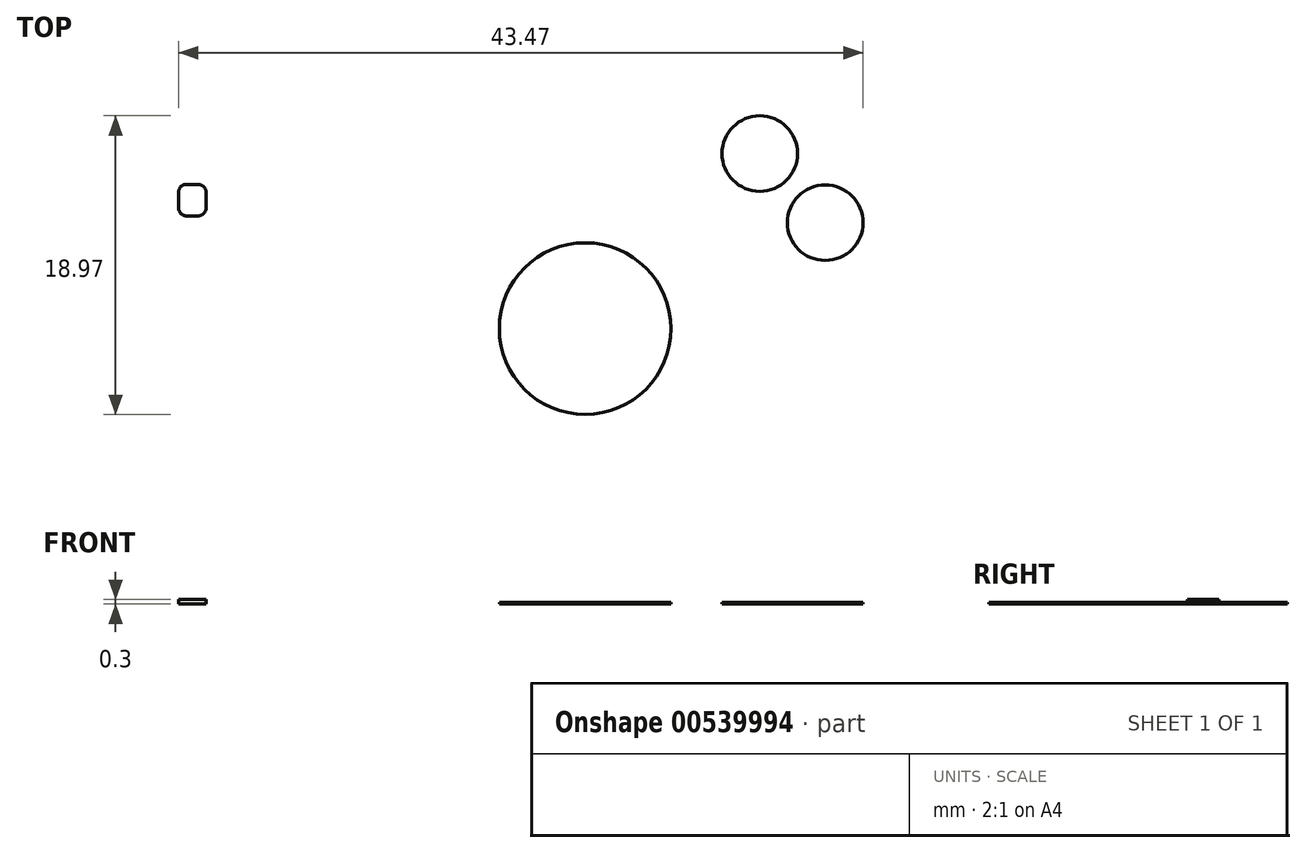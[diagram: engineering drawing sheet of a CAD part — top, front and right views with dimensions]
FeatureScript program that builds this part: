
annotation { "Feature Type Name" : "Feature", "Feature Type Description" : "" }
export const myFeature = defineFeature(function(context is Context, id is Id, definition is map)
    precondition{}
    {
        {
            var Q0;
            Q0=qCreatedBy(makeId("Top.planeOp"),FACE);
            var sketch = newSketch(context, id + "F0", { "sketchPlane" : qUnion([Q0])});
            skCircle(sketch, "E0", {"center": v(0, 0) * mm, "radius": 5.45 * mm});
            skSolve(sketch);
        }
        {
            var Q0;
            Q0 = qSketchRegion(id + "F0", true);
            extrude(context, id + "F1", {"entities" : qUnion([Q0]), "depth" : .1 * mm, "offsetDistance" : 25 * mm});
        }
        {
            var Q0;
            Q0=qCreatedBy(makeId("Top.planeOp"),FACE);
            var sketch = newSketch(context, id + "F2", { "sketchPlane" : qUnion([Q0])});
            skCircle(sketch, "E1", {"center": v(11.1, 11.12) * mm, "radius": 2.4 * mm});
            skCircle(sketch, "E2", {"center": v(15.25, 6.73) * mm, "radius": 2.4 * mm});
            skSolve(sketch);
        }
        {
            var Q0;
            Q0=makeQuery(id+"F2.imprint","IMPRINT",FACE,{"disambiguationData":[TD([[makeQuery(id+"F2.imprint","IMPRINT",EDGE,{"derivedFrom":sQuery(id+"F2.wireOp",EDGE,"E1")}),1.0]])]});
            var Q1;
            Q1=makeQuery(id+"F2.imprint","IMPRINT",FACE,{"disambiguationData":[TD([[makeQuery(id+"F2.imprint","IMPRINT",EDGE,{"derivedFrom":sQuery(id+"F2.wireOp",EDGE,"E2")}),1.0]])]});
            extrude(context, id + "F3", {"entities" : qUnion([Q0, Q1]), "depth" : .1 * mm, "offsetDistance" : 25 * mm});
        }
        {
            var Q0;
            Q0=qCreatedBy(makeId("Top.planeOp"),FACE);
            var sketch = newSketch(context, id + "F4", { "sketchPlane" : qUnion([Q0])});
            skLineSegment(sketch, "E3.bottom", {"start": v(-24.07, 7.16) * mm, "end": v(-25.82, 7.16) * mm});
            skLineSegment(sketch, "E3.top", {"start": v(-24.07, 9.16) * mm, "end": v(-25.82, 9.16) * mm});
            skLineSegment(sketch, "E3.left", {"start": v(-24.07, 7.16) * mm, "end": v(-24.07, 9.16) * mm});
            skLineSegment(sketch, "E3.right", {"start": v(-25.82, 7.16) * mm, "end": v(-25.82, 9.16) * mm});
            skPoint(sketch, "E3.middle", {"position": v(-24.95, 8.16) * mm});
            skLineSegment(sketch, "E4.bottom", {"start": v(-25.82, 9.16) * mm, "end": v(-24.07, 9.16) * mm});
            skLineSegment(sketch, "E4.top", {"start": v(-25.82, 10.56) * mm, "end": v(-24.07, 10.56) * mm});
            skLineSegment(sketch, "E4.left", {"start": v(-25.82, 9.16) * mm, "end": v(-25.82, 10.56) * mm});
            skLineSegment(sketch, "E4.right", {"start": v(-24.07, 9.16) * mm, "end": v(-24.07, 10.56) * mm});
            skLineSegment(sketch, "E5.bottom", {"start": v(-25.82, 7.16) * mm, "end": v(-24.07, 7.16) * mm});
            skLineSegment(sketch, "E5.top", {"start": v(-25.82, 5.76) * mm, "end": v(-24.07, 5.76) * mm});
            skLineSegment(sketch, "E5.left", {"start": v(-25.82, 7.16) * mm, "end": v(-25.82, 5.76) * mm});
            skLineSegment(sketch, "E5.right", {"start": v(-24.07, 7.16) * mm, "end": v(-24.07, 5.76) * mm});
            skSolve(sketch);
        }
        {
            var Q0;
            Q0=makeQuery(id+"F4.imprint","IMPRINT",FACE,{"disambiguationData":[TD([[makeQuery(id+"F4.imprint","IMPRINT",EDGE,{"derivedFrom":sQuery(id+"F4.wireOp",EDGE,"E4.bottom")}),1.0]])]});
            var Q1;
            Q1=makeQuery(id+"F4.imprint","IMPRINT",FACE,{"disambiguationData":[TD([[makeQuery(id+"F4.imprint","IMPRINT",EDGE,{"derivedFrom":sQuery(id+"F4.wireOp",EDGE,"E3.left")}),1.0]])]});
            var Q2;
            Q2=makeQuery(id+"F4.imprint","IMPRINT",FACE,{"disambiguationData":[TD([[makeQuery(id+"F4.imprint","IMPRINT",EDGE,{"derivedFrom":sQuery(id+"F4.wireOp",EDGE,"E5.bottom")}),-1.0]])]});
            extrude(context, id + "F5", {"entities" : qUnion([Q0, Q1, Q2]), "depth" : .3 * mm, "offsetDistance" : 25 * mm});
        }
        {
            var Q0;
            Q0=makeQuery(id+"F5.opExtrude","SWEPT_EDGE",EDGE,{"disambiguationData":[OSD([sQuery(id+"F4.wireOp",EDGE,"E4.top"),sQuery(id+"F4.wireOp",EDGE,"E4.right")])]});
            var Q1;
            Q1=makeQuery(id+"F5.opExtrude","SWEPT_EDGE",EDGE,{"disambiguationData":[OSD([sQuery(id+"F4.wireOp",EDGE,"E4.top"),sQuery(id+"F4.wireOp",EDGE,"E4.left")])]});
            var Q2;
            Q2=makeQuery(id+"F5.opExtrude","SWEPT_EDGE",EDGE,{"disambiguationData":[OSD([sQuery(id+"F4.wireOp",EDGE,"E5.top"),sQuery(id+"F4.wireOp",EDGE,"E5.left")])]});
            var Q3;
            Q3=makeQuery(id+"F5.opExtrude","SWEPT_EDGE",EDGE,{"disambiguationData":[OSD([sQuery(id+"F4.wireOp",EDGE,"E5.top"),sQuery(id+"F4.wireOp",EDGE,"E5.right")])]});
            fillet(context, id + "F6", {"entities" : qUnion([Q0, Q1, Q2, Q3]), "radius" : .5 * mm, "tangentPropagation" : true, "allowEdgeOverflow" : false});
        }
    });
